# Revit family: KS ALU-PU 80, DS 30, m.Blz, M16, Ø219,1-355,6
name_source: partatom
category: HLS-Bauteile
units: mm (PartAtom-declared; Revit-internal decimal feet)

## family parameters
Arbeitsebenenbasiert = Ja
Beim Laden mit Abzugskörper schneiden = Nein
Bemaßung runder Anschluss = Durchmesser verwenden
Beschriftungsausrichtung beibehalten = Nein
Gemeinsam genutzt = Ja
Immer vertikal = Nein
Raumberechnungspunkt = Nein
Teiletyp = Normal

## types (4) — shared parameters
A = 50 mm  [stored 0.164042 ft]
Anschluss = M16
Anschlußhöhe = 55 mm
Baustoffklasse = B2
DF2 = 20 mm  [stored 0.0656168 ft]
DS = 30 mm  [stored 0.0984252 ft]
DVS = 13 mm
Dichte Kern = 80 kg/m³
Dichte Mantel = 2700 kg/m³
Dicke Mantel = 0.08 mm
Druckverteilung = Blechzylinder
Dämmkörper = ALU/PU
Dämmstärke = 30 mm  [stored 0.0984252 ft]
Fabrikat = MEFA
Firma = MEFA Befestigungs- und Montagesysteme GmbH
HGA = 15 mm  [stored 0.0492126 ft]
Kurztext1 = Kälteschelle RG80 ALU/PU
L = 100 mm  [stored 0.328084 ft]
MB = 50 mm  [stored 0.164042 ft]
MD = 5 mm  [stored 0.0164042 ft]
Material = Stahl
Material Mantel = Alufolie
Materialname = S235
Mengeneinheit = St
Oberflaeche = galvanisch verzinkt
Rohrschellentyp = Titan HD
Schalenlänge = 100 mm
Vorgabe-Ansicht = 1219 mm
Wasserdampfdiffusionswiderstand = 18750 µ
Wärmeleitfähigkeit = 0.025 W/mK
max. Temperaturbeständigkeit = 120 °C
mittl. Nenndruckfestigkeit Kern = 0,5 N/mm²
stat. Belastung Kern = 0,1 N/mm²
vpe = 1
zero-valued in all types: AB

## per-type parameters (varying)
| type | Artikelnummer | B | Breite | D | D0 | DF1 | EAN | Gewicht | Gewicht pro Bauteil | H | Kurztext2 | R | RM | Rohraußendurchmesser Stahl | S | max. zul. Last |
| Kälteschelle ALU-PU 80, DS 30, m.Blz, M16, Ø219,1 | 7592193/B | 363 mm | 364 mm  [stored 1.19423 ft] | 219 mm | 279 mm | 21 mm  [stored 0.0688976 ft] | 4250928444349 | 2.82 kg | 2.82 kg | 304 mm | 219,1 mm Iso 30 x 100 mm M16 | 140 mm | 145 mm | 219,1 mm | 342 mm | 3.20 kN |
| Kälteschelle ALU-PU 80, DS 30, m.Blz, M16, Ø273 | 7592733/B | 415 mm  [stored 1.36155 ft] | 416 mm | 273 mm  [stored 0.895669 ft] | 333 mm | 19 mm  [stored 0.062336 ft] | 4250928444363 | 3.27 kg | 3.27 kg | 358 mm | 273 mm Iso 30 x 100 mm M16 | 167 mm | 172 mm | 273 mm | 396 mm  [stored 1.29921 ft] | 3.90 kN |
| Kälteschelle ALU-PU 80, DS 30, m.Blz, M16, Ø323,9 | 7593243/B | 467 mm  [stored 1.53215 ft] | 467 mm  [stored 1.53215 ft] | 324 mm | 384 mm | 20 mm  [stored 0.0656168 ft] | 4250928444387 | 3.72 kg | 3.72 kg | 409 mm | 323,9 mm Iso 30 x 100 mm M16 | 192 mm | 197 mm | 323,9 mm | 447 mm | 4.50 kN |
| Kälteschelle ALU-PU 80, DS 30, m.Blz, M16, Ø355,6 | 7593563/B | 498 mm | 495 mm  [stored 1.62402 ft] | 356 mm | 416 mm | 20 mm  [stored 0.0656168 ft] | 4250928444400 | 3.42 kg | 3.42 kg | 441 mm | 355,6 mm Iso 30 x 100 mm M16 | 208 mm | 213 mm | 355,6 mm | 479 mm | 4.90 kN |

note: [stored X ft] marks values corroborated as IEEE doubles in the binary element streams (Revit-internal decimal feet)

## geometry (parser evidence)
native form markers: Sweep x5
no freeform markers — native parametric forms only
